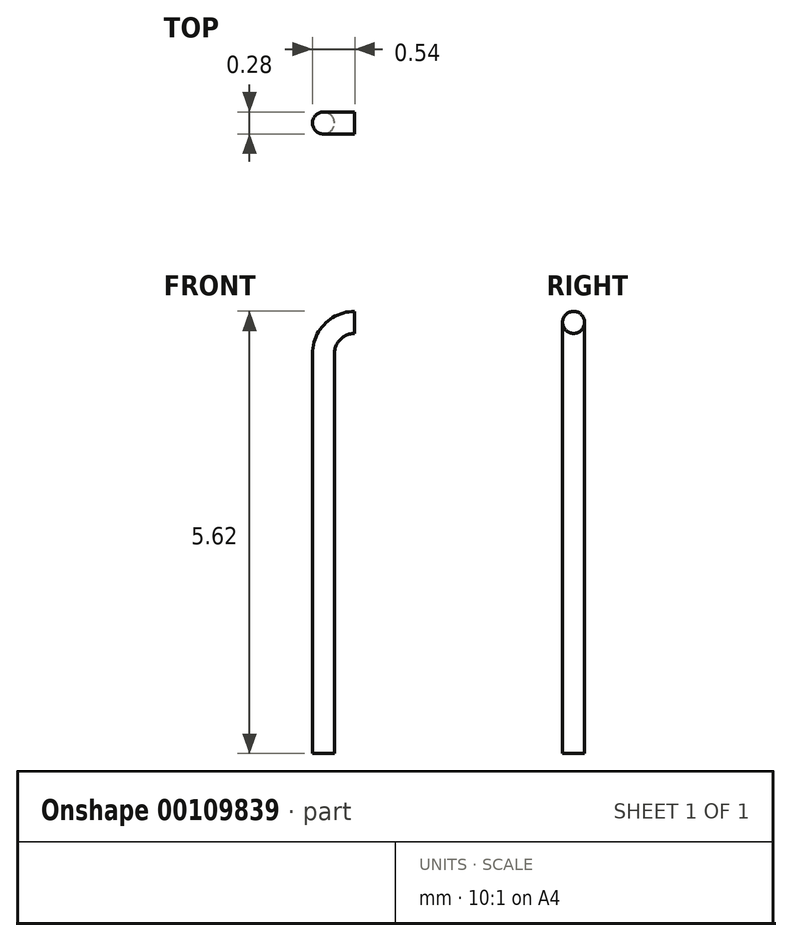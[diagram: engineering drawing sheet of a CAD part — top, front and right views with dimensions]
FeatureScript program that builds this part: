
annotation { "Feature Type Name" : "Feature", "Feature Type Description" : "" }
export const myFeature = defineFeature(function(context is Context, id is Id, definition is map)
    precondition{}
    {
        {
            var Q0;
            Q0=qCreatedBy(makeId("Top.planeOp"),FACE);
            var sketch = newSketch(context, id + "F0", { "sketchPlane" : qUnion([Q0])});
            skCircle(sketch, "E0", {"center": v(0, 0) * mm, "radius": 0.14 * mm});
            skSolve(sketch);
        }
        {
            var Q0;
            Q0=qCreatedBy(makeId("Front.planeOp"),FACE);
            var sketch = newSketch(context, id + "F1", { "sketchPlane" : qUnion([Q0])});
            skArc(sketch, "E1", {"start": v(0, 0) * mm, "mid": v(0.12, 0.28) * mm, "end": v(0.4, 0.4) * mm});
            skSolve(sketch);
        }
        {
            var Q0;
            Q0 = qSketchRegion(id + "F0", true);
            var Q1;
            Q1 = qConstructionFilter(qBodyType(qCreatedBy(id + "F1" ,EDGE), BodyType.WIRE), ConstructionObject.NO);
            sweep(context, id + "F2", {"profiles" : qUnion([Q0]), "path" : qUnion([Q1])});
        }
        {
            var Q0;
            Q0=makeQuery(id+"F2.opSweep","CAP_FACE",FACE,{"disambiguationData":[OSD([sQuery(id+"F0.wireOp",EDGE,"E0"),sQuery(id+"F1.wireOp",VERTEX,"E1.start")])],"isStart":true});
            extrude(context, id + "F3", {"entities" : qUnion([Q0]), "operationType" : NewBodyOperationType.ADD, "depth" : 5.08 * mm});
        }
    });
